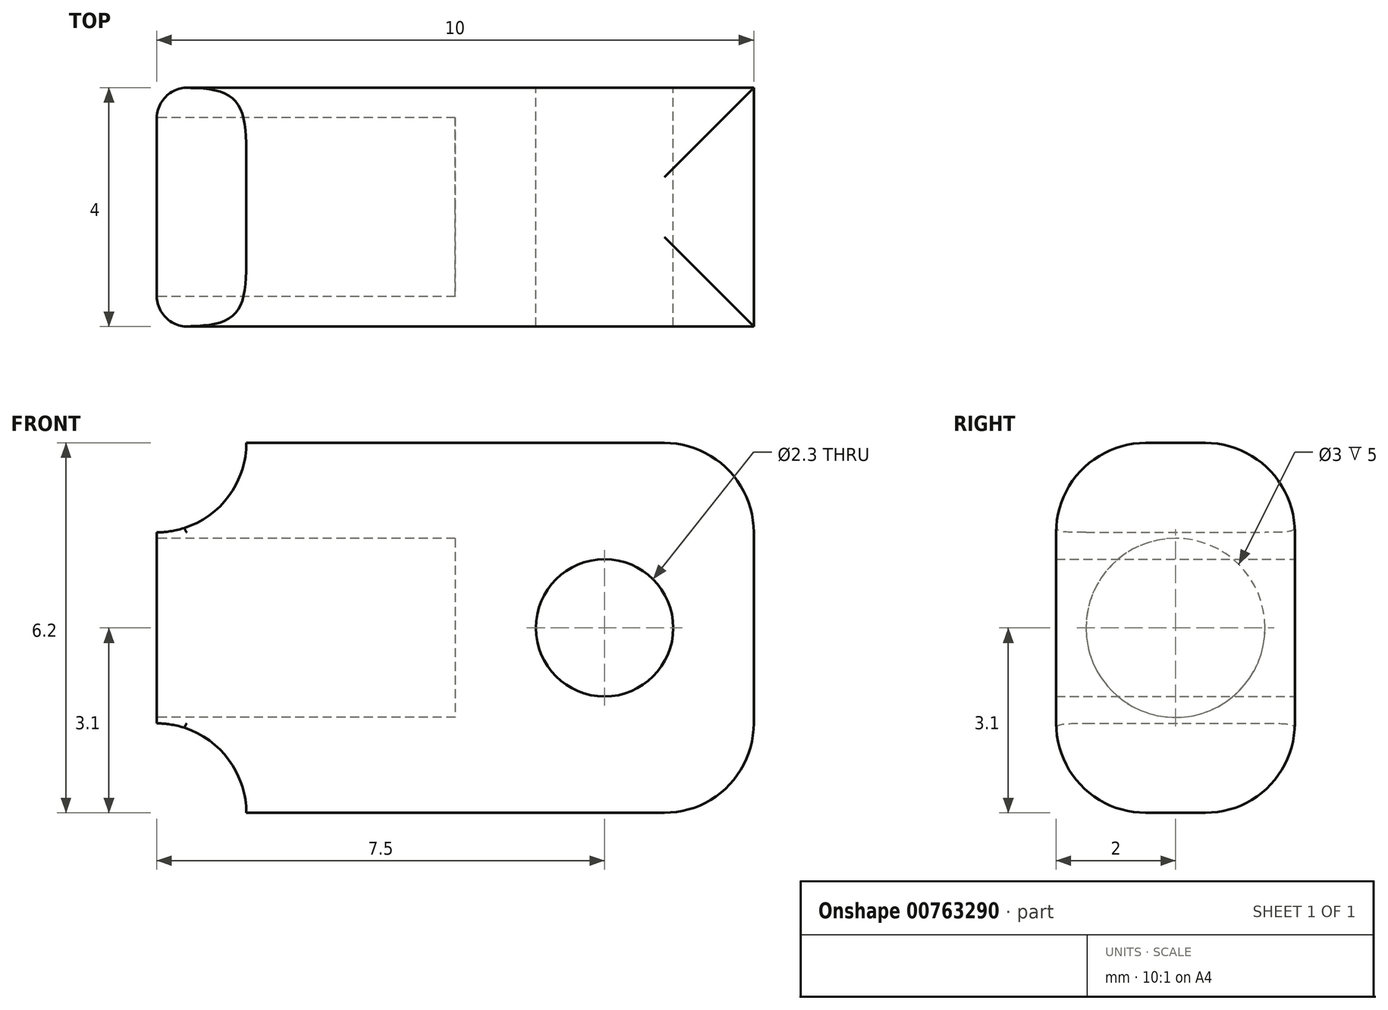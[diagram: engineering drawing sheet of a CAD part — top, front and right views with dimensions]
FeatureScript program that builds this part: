
annotation { "Feature Type Name" : "Feature", "Feature Type Description" : "" }
export const myFeature = defineFeature(function(context is Context, id is Id, definition is map)
    precondition{}
    {
        {
            var Q0;
            Q0=qCreatedBy(makeId("Front.planeOp"),FACE);
            var sketch = newSketch(context, id + "F0", { "sketchPlane" : qUnion([Q0])});
            skLineSegment(sketch, "E0.bottom", {"start": v(-3.5, 3.1) * mm, "end": v(5, 3.1) * mm});
            skLineSegment(sketch, "E0.top", {"start": v(-3.5, -3.1) * mm, "end": v(5, -3.1) * mm});
            skLineSegment(sketch, "E0.left", {"start": v(-5, 1.6) * mm, "end": v(-5, -1.6) * mm});
            skLineSegment(sketch, "E0.right", {"start": v(5, 3.1) * mm, "end": v(5, -3.1) * mm});
            skPoint(sketch, "E0.middle", {"position": v(0, 0) * mm});
            skArc(sketch, "E1", {"start": v(-5, 1.6) * mm, "mid": v(-3.94, 2.04) * mm, "end": v(-3.5, 3.1) * mm});
            skArc(sketch, "E2", {"start": v(-3.5, -3.1) * mm, "mid": v(-3.94, -2.04) * mm, "end": v(-5, -1.6) * mm});
            skCircle(sketch, "E3", {"center": v(2.5, 0) * mm, "radius": 1.15 * mm});
            skSolve(sketch);
        }
        {
            var Q0;
            Q0 = qSketchRegion(id + "F0", true);
            extrude(context, id + "F1", {"entities" : qUnion([Q0]), "depth" : 4 * mm, "offsetDistance" : 25 * mm});
        }
        {
            var Q0;
            Q0=makeQuery(id+"F1.opExtrude","SWEPT_FACE",FACE,{"disambiguationData":[OSD([sQuery(id+"F0.wireOp",EDGE,"E0.left")])]});
            var sketch = newSketch(context, id + "F2", { "sketchPlane" : qUnion([Q0])});
            skCircle(sketch, "E4", {"center": v(2, 0) * mm, "radius": 1.5 * mm});
            skSolve(sketch);
        }
        {
            var Q0;
            Q0=makeQuery(id+"F2.imprint","IMPRINT",FACE,{"disambiguationData":[TD([[makeQuery(id+"F2.imprint","IMPRINT",EDGE,{"derivedFrom":sQuery(id+"F2.wireOp",EDGE,"E4")}),1.0]])]});
            extrude(context, id + "F3", {"entities" : qUnion([Q0]), "operationType" : NewBodyOperationType.REMOVE, "oppositeDirection" : true, "depth" : 5 * mm, "offsetDistance" : 25 * mm});
        }
        {
            var Q0;
            Q0=makeQuery(id+"F1.opExtrude","CAP_EDGE",EDGE,{"disambiguationData":[OSD([sQuery(id+"F0.wireOp",EDGE,"E0.bottom")])],"isStart":false});
            var Q1;
            Q1=makeQuery(id+"F1.opExtrude","CAP_EDGE",EDGE,{"disambiguationData":[OSD([sQuery(id+"F0.wireOp",EDGE,"E0.bottom")])],"isStart":true});
            var Q2;
            Q2=makeQuery(id+"F1.opExtrude","CAP_EDGE",EDGE,{"disambiguationData":[OSD([sQuery(id+"F0.wireOp",EDGE,"E0.top")])],"isStart":false});
            var Q3;
            Q3=makeQuery(id+"F1.opExtrude","CAP_EDGE",EDGE,{"disambiguationData":[OSD([sQuery(id+"F0.wireOp",EDGE,"E0.top")])],"isStart":true});
            var Q4;
            Q4=makeQuery(id+"F1.opExtrude","SWEPT_EDGE",EDGE,{"disambiguationData":[OSD([sQuery(id+"F0.wireOp",EDGE,"E0.bottom"),sQuery(id+"F0.wireOp",EDGE,"E0.right")])]});
            var Q5;
            Q5=makeQuery(id+"F1.opExtrude","SWEPT_EDGE",EDGE,{"disambiguationData":[OSD([sQuery(id+"F0.wireOp",EDGE,"E0.top"),sQuery(id+"F0.wireOp",EDGE,"E0.right")])]});
            fillet(context, id + "F4", {"entities" : qUnion([Q0, Q1, Q2, Q3, Q4, Q5]), "radius" : 1.5 * mm, "tangentPropagation" : true, "allowEdgeOverflow" : false});
        }
        {
            var Q0;
            Q0=makeQuery(id+"F1.opExtrude","CAP_EDGE",EDGE,{"disambiguationData":[OSD([sQuery(id+"F0.wireOp",EDGE,"E0.left")])],"isStart":false});
            var Q1;
            Q1=makeQuery(id+"F1.opExtrude","CAP_EDGE",EDGE,{"disambiguationData":[OSD([sQuery(id+"F0.wireOp",EDGE,"E0.left")])],"isStart":true});
            fillet(context, id + "F5", {"entities" : qUnion([Q0, Q1]), "radius" : .5 * mm, "tangentPropagation" : true, "allowEdgeOverflow" : false});
        }
    });
